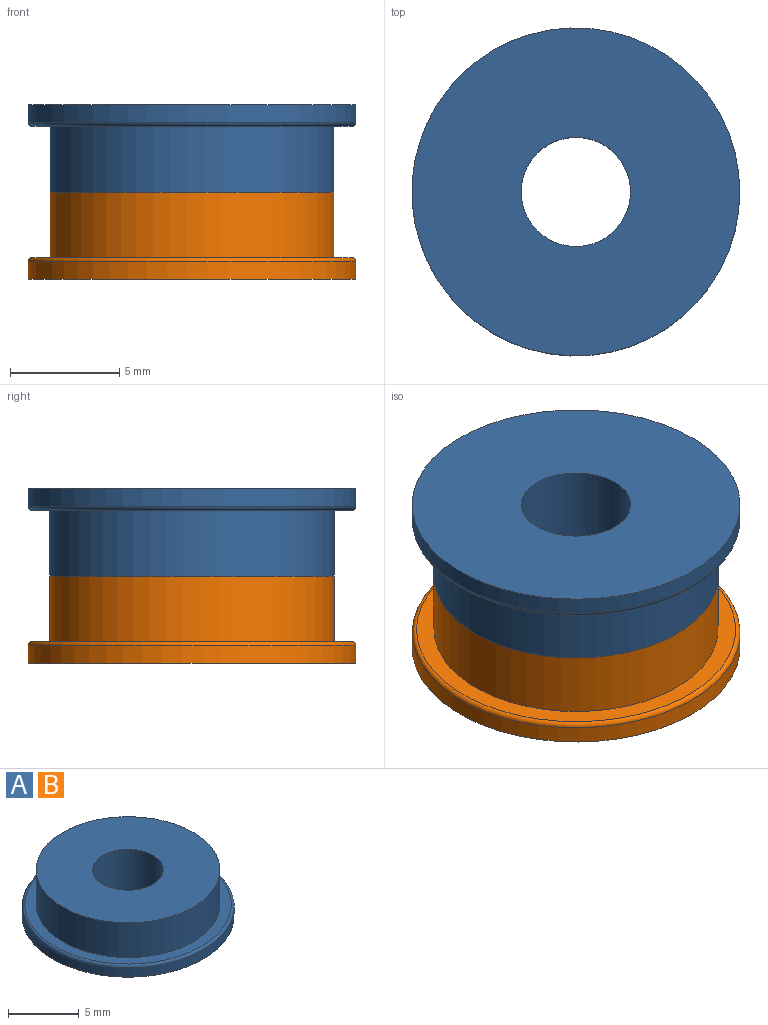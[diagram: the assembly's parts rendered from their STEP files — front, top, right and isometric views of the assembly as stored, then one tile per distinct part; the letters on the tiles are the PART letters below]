
ASSEMBLY  parts=2 mates=1
PART A: 7 faces, bbox 16.2x16.2x4 mm
  f0: cylinder r=2.5mm len=5mm, axis (0,0,-1), area 62.8mm2, adj f3,f5
  f1: cylinder r=7.5mm len=15mm, axis (0,0,-1), area 37.7mm2, adj f3,f6
  f2: plane 14.6x14.6mm, normal (0,0,1), area 34.7mm2, adj f4,f6
  f3: plane 15x15mm, normal (0,0,-1), area 157.1mm2, adj f0,f1
  f4: cylinder r=6.5mm len=13mm, axis (0,0,-1), area 122.5mm2, adj f2,f5
  f5: plane 13x13mm, normal (0,0,1), area 113.1mm2, adj f0,f4
  f6: torus R=7.3mm, axis (0,0,1), area 14.7mm2, adj f1,f2
PART B: same geometry as A
PLACE A rot(axis=(1,0,0),180deg) t=(12.12,4.03,-4.95)mm
PLACE B t=(12.12,4.03,-12.95)mm
MATE fastened A.f0 <-> B.f0  axis (0,0,-1) through (12.12,4.03,-8.95)mm
